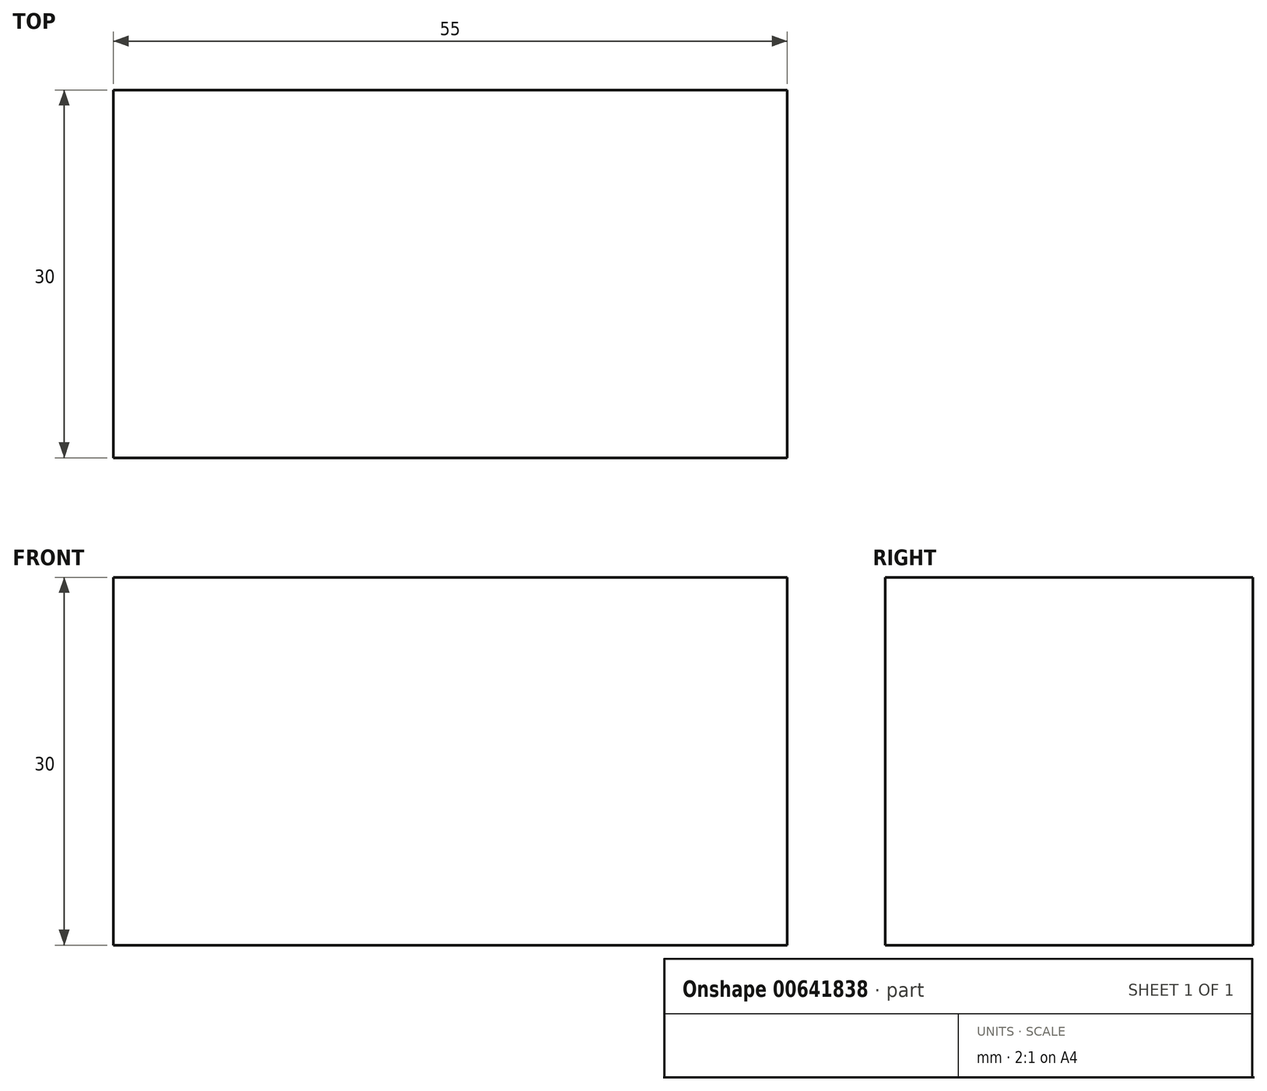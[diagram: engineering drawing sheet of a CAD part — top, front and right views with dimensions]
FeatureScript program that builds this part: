
annotation { "Feature Type Name" : "Feature", "Feature Type Description" : "" }
export const myFeature = defineFeature(function(context is Context, id is Id, definition is map)
    precondition{}
    {
        {
            var Q0;
            Q0=qCreatedBy(makeId("Top.planeOp"),FACE);
            var sketch = newSketch(context, id + "F0", { "sketchPlane" : qUnion([Q0])});
            skLineSegment(sketch, "E0.bottom", {"start": v(27.5, -15) * mm, "end": v(-27.5, -15) * mm});
            skLineSegment(sketch, "E0.top", {"start": v(27.5, 15) * mm, "end": v(-27.5, 15) * mm});
            skLineSegment(sketch, "E0.left", {"start": v(27.5, -15) * mm, "end": v(27.5, 15) * mm});
            skLineSegment(sketch, "E0.right", {"start": v(-27.5, -15) * mm, "end": v(-27.5, 15) * mm});
            skPoint(sketch, "E0.middle", {"position": v(0, 0) * mm});
            skSolve(sketch);
        }
        {
            var Q0;
            Q0=makeQuery(id+"F0.imprint","IMPRINT",FACE,{"disambiguationData":[TD([[makeQuery(id+"F0.imprint","IMPRINT",EDGE,{"derivedFrom":sQuery(id+"F0.wireOp",EDGE,"E0.bottom")}),-1.0]])]});
            extrude(context, id + "F1", {"entities" : qUnion([Q0]), "depth" : 30 * mm, "offsetDistance" : 25 * mm});
        }
    });
